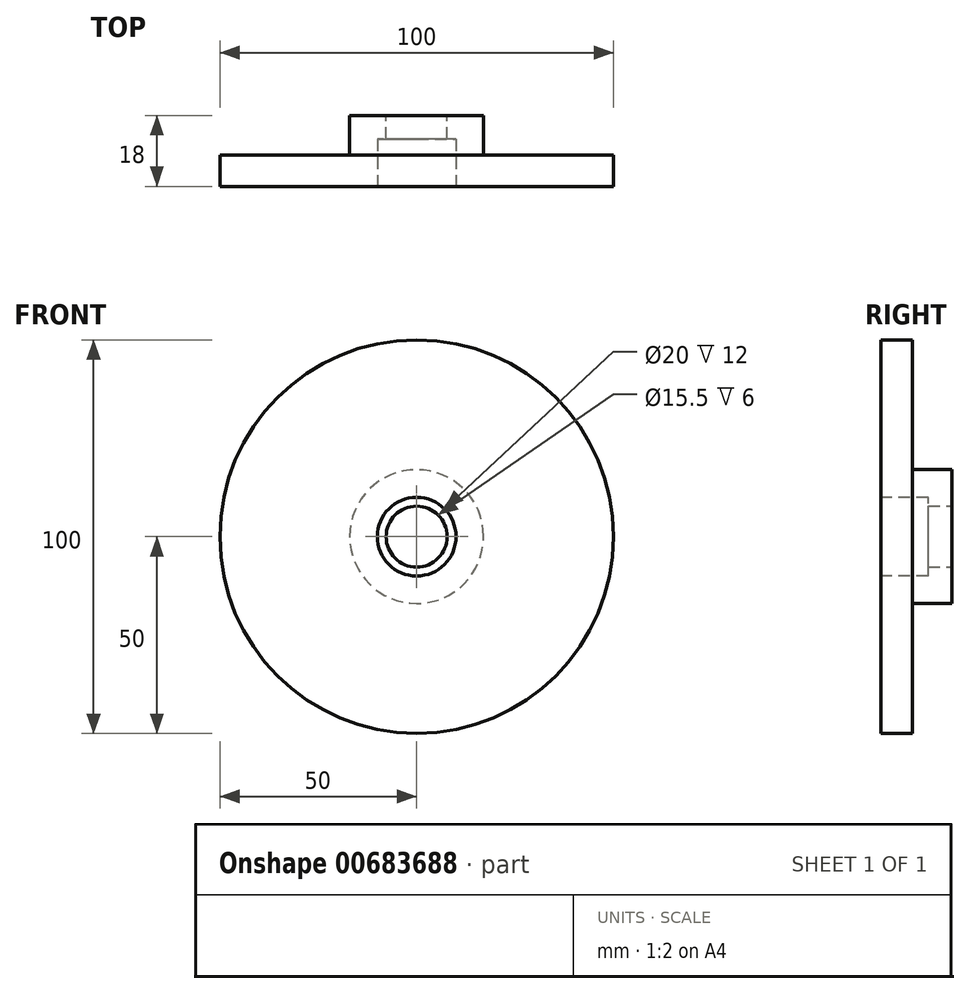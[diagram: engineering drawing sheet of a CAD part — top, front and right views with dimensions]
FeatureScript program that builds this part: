
annotation { "Feature Type Name" : "Feature", "Feature Type Description" : "" }
export const myFeature = defineFeature(function(context is Context, id is Id, definition is map)
    precondition{}
    {
        {
            var Q0;
            Q0=qCreatedBy(makeId("Front.planeOp"),FACE);
            var sketch = newSketch(context, id + "F0", { "sketchPlane" : qUnion([Q0])});
            skCircle(sketch, "E0", {"center": v(0, 0) * mm, "radius": 50 * mm});
            skSolve(sketch);
        }
        {
            var Q0;
            Q0 = qSketchRegion(id + "F0", true);
            extrude(context, id + "F1", {"entities" : qUnion([Q0]), "depth" : 43 * mm, "offsetDistance" : 25 * mm});
        }
        {
            var Q0;
            Q0=makeQuery(id+"F1.opExtrude","CAP_FACE",FACE,{"disambiguationData":[OSD([sQuery(id+"F0.wireOp",EDGE,"E0")])],"isStart":true});
            var sketch = newSketch(context, id + "F2", { "sketchPlane" : qUnion([Q0])});
            skCircle(sketch, "E1", {"center": v(0, 0) * mm, "radius": 17 * mm});
            skCircle(sketch, "E2", {"center": v(0, 0) * mm, "radius": 144.37 * mm});
            skSolve(sketch);
        }
        {
            var Q0;
            Q0=makeQuery(id+"F2.imprint","IMPRINT",FACE,{"disambiguationData":[TD([[makeQuery(id+"F2.imprint","IMPRINT",EDGE,{"derivedFrom":sQuery(id+"F2.wireOp",EDGE,"E1")}),-1.0]])]});
            var Q1;
            Q1=makeQuery(id+"F2.imprint","IMPRINT",FACE,{"disambiguationData":[TD([[makeQuery(id+"F2.imprint","IMPRINT",EDGE,{"derivedFrom":sQuery(id+"F2.wireOp",EDGE,"E2")}),1.0]])]});
            extrude(context, id + "F3", {"entities" : qUnion([Q0, Q1]), "operationType" : NewBodyOperationType.REMOVE, "oppositeDirection" : true, "depth" : 10 * mm, "offsetDistance" : 25 * mm});
        }
        {
            var Q0;
            Q0=makeQuery(id+"F1.opExtrude","CAP_FACE",FACE,{"disambiguationData":[OSD([sQuery(id+"F0.wireOp",EDGE,"E0")])],"isStart":false});
            var sketch = newSketch(context, id + "F4", { "sketchPlane" : qUnion([Q0])});
            skCircle(sketch, "E3", {"center": v(0, 0) * mm, "radius": 61.76 * mm});
            skSolve(sketch);
        }
        {
            var Q0;
            Q0 = qSketchRegion(id + "F4", true);
            extrude(context, id + "F5", {"entities" : qUnion([Q0]), "operationType" : NewBodyOperationType.REMOVE, "oppositeDirection" : true, "depth" : 25 * mm, "offsetDistance" : 25 * mm});
        }
        {
            var Q0;
            Q0=makeQuery(id+"F5.boolean.opBoolean","COPY",FACE,{"derivedFrom":makeQuery(id+"F5.opExtrude","CAP_FACE",FACE,{"disambiguationData":[OSD([sQuery(id+"F4.wireOp",EDGE,"E3")])],"isStart":false})});
            var sketch = newSketch(context, id + "F6", { "sketchPlane" : qUnion([Q0])});
            skCircle(sketch, "E4", {"center": v(0, 0) * mm, "radius": 10 * mm});
            skSolve(sketch);
        }
        {
            var Q0;
            Q0 = qSketchRegion(id + "F6", true);
            extrude(context, id + "F7", {"entities" : qUnion([Q0]), "operationType" : NewBodyOperationType.REMOVE, "oppositeDirection" : true, "depth" : 12 * mm, "offsetDistance" : 25 * mm});
        }
        {
            var Q0;
            Q0=qCreatedBy(makeId("Front.planeOp"),FACE);
            var sketch = newSketch(context, id + "F8", { "sketchPlane" : qUnion([Q0])});
            skCircle(sketch, "E5", {"center": v(0, 0) * mm, "radius": 7.75 * mm});
            skSolve(sketch);
        }
        {
            var Q0;
            Q0 = qSketchRegion(id + "F8", true);
            extrude(context, id + "F9", {"entities" : qUnion([Q0]), "operationType" : NewBodyOperationType.REMOVE, "depth" : 179 * mm, "offsetDistance" : 25 * mm});
        }
    });
